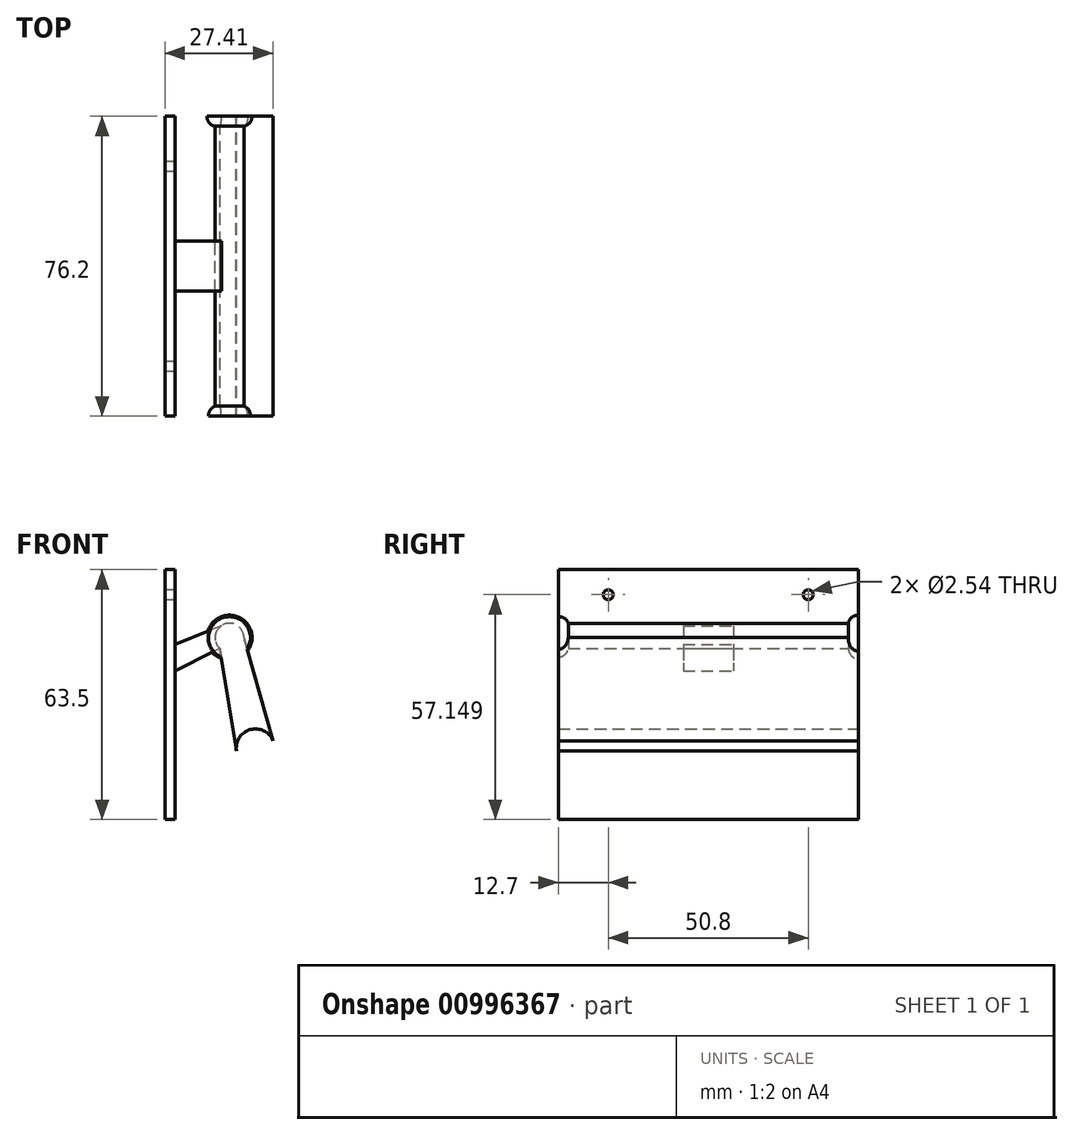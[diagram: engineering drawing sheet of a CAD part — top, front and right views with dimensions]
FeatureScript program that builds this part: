
annotation { "Feature Type Name" : "Feature", "Feature Type Description" : "" }
export const myFeature = defineFeature(function(context is Context, id is Id, definition is map)
    precondition{}
    {
        {
            var Q0;
            Q0=qCreatedBy(makeId("Front.planeOp"),FACE);
            var sketch = newSketch(context, id + "F0", { "sketchPlane" : qUnion([Q0])});
            skLineSegment(sketch, "E0.bottom", {"start": v(-19.93, 54.34) * mm, "end": v(-17.39, 54.34) * mm});
            skLineSegment(sketch, "E0.top", {"start": v(-19.93, -9.16) * mm, "end": v(-17.39, -9.16) * mm});
            skLineSegment(sketch, "E0.left", {"start": v(-19.93, 54.34) * mm, "end": v(-19.93, -9.16) * mm});
            skLineSegment(sketch, "E0.right", {"start": v(-17.39, 54.34) * mm, "end": v(-17.39, -9.16) * mm});
            skCircle(sketch, "E1", {"center": v(-3.57, 37.05) * mm, "radius": 3.67 * mm});
            skCircle(sketch, "E2", {"center": v(3, 9.03) * mm, "radius": 4.85 * mm});
            skLineSegment(sketch, "E3", {"start": v(0.1, 37.05) * mm, "end": v(7.78, 9.8) * mm});
            skLineSegment(sketch, "E4", {"start": v(-6.03, 34.33) * mm, "end": v(-1.53, 6.59) * mm});
            skLineSegment(sketch, "E5", {"start": v(-5.63, 40.09) * mm, "end": v(-17.39, 35.29) * mm});
            skLineSegment(sketch, "E6", {"start": v(-6.03, 34.33) * mm, "end": v(-17.39, 28.66) * mm});
            skSolve(sketch);
        }
        {
            var Q0;
            {var subQ1=sQuery(id+"F0.wireOp",EDGE,"E0.bottom");Q0=makeQuery(id+"F0.imprint","IMPRINT",FACE,{"disambiguationData":[TD([[makeQuery(id+"F0.imprint","IMPRINT",EDGE,{"derivedFrom":subQ1}),-1.0]])]});}
            var Q1;
            {var subQ0=sQuery(id+"F0.wireOp",EDGE,"E1");var subQ1=makeQuery(id+"F0.imprint","INTERSECT",VERTEX,{"derivedFrom":[subQ0,sQuery(id+"F0.wireOp",EDGE,"E3")]});Q1=makeQuery(id+"F0.imprint","IMPRINT",FACE,{"disambiguationData":[TD([[makeQuery(id+"F0.imprint","IMPRINT",EDGE,{"disambiguationData":[TD([[subQ1,-1.0]])],"derivedFrom":subQ0}),1.0]])]});}
            var Q2;
            {var subQ3=sQuery(id+"F0.wireOp",EDGE,"E4");var subQ5=sQuery(id+"F0.wireOp",EDGE,"E2");var subQ6=makeQuery(id+"F0.imprint","INTERSECT",VERTEX,{"derivedFrom":[subQ5,subQ3]});Q2=makeQuery(id+"F0.imprint","IMPRINT",FACE,{"disambiguationData":[TD([[makeQuery(id+"F0.imprint","IMPRINT",EDGE,{"disambiguationData":[TD([[subQ6,1.0]])],"derivedFrom":subQ5}),-1.0]])]});}
            extrude(context, id + "F1", {"entities" : qUnion([Q0, Q1, Q2]), "endBound" : BoundingType.SYMMETRIC, "depth" : 76.2 * mm, "offsetDistance" : 25.4 * mm});
        }
        {
            var Q0;
            {var subQ0=sQuery(id+"F0.wireOp",EDGE,"E5");Q0=makeQuery(id+"F0.imprint","IMPRINT",FACE,{"disambiguationData":[TD([[makeQuery(id+"F0.imprint","IMPRINT",EDGE,{"derivedFrom":subQ0}),1.0]])]});}
            extrude(context, id + "F2", {"entities" : qUnion([Q0]), "endBound" : BoundingType.SYMMETRIC, "depth" : 12.7 * mm, "offsetDistance" : 25.4 * mm});
        }
        {
            var Q0;
            Q0=makeQuery(id+"F1.opExtrude","SWEPT_FACE",FACE,{"disambiguationData":[OSD([sQuery(id+"F0.wireOp",EDGE,"E0.right")])]});
            var sketch = newSketch(context, id + "F3", { "sketchPlane" : qUnion([Q0])});
            skCircle(sketch, "E7", {"center": v(-25.4, 47.99) * mm, "radius": 1.27 * mm});
            skCircle(sketch, "E8", {"center": v(25.4, 47.99) * mm, "radius": 1.27 * mm});
            skSolve(sketch);
        }
        {
            var Q0;
            Q0=makeQuery(id+"F3.imprint","IMPRINT",FACE,{"disambiguationData":[TD([[makeQuery(id+"F3.imprint","IMPRINT",EDGE,{"derivedFrom":sQuery(id+"F3.wireOp",EDGE,"E7")}),1.0]])]});
            var Q1;
            Q1=sQuery(id+"F3.wireOp",EDGE,"E7");
            extrude(context, id + "F4", {"entities" : qUnion([Q0]), "operationType" : NewBodyOperationType.REMOVE, "surfaceEntities" : qUnion([Q1]), "endBound" : BoundingType.THROUGH_ALL, "oppositeDirection" : true, "depth" : 25.4 * mm, "offsetDistance" : 25.4 * mm});
        }
        {
            var Q0;
            Q0=makeQuery(id+"F3.imprint","IMPRINT",FACE,{"disambiguationData":[TD([[makeQuery(id+"F3.imprint","IMPRINT",EDGE,{"derivedFrom":sQuery(id+"F3.wireOp",EDGE,"E8")}),1.0]])]});
            var Q1;
            Q1=sQuery(id+"F3.wireOp",EDGE,"E8");
            extrude(context, id + "F5", {"entities" : qUnion([Q0]), "operationType" : NewBodyOperationType.REMOVE, "surfaceEntities" : qUnion([Q1]), "endBound" : BoundingType.THROUGH_ALL, "oppositeDirection" : true, "depth" : 25.4 * mm, "offsetDistance" : 25.4 * mm});
        }
        {
            var Q0;
            Q0=makeQuery(id+"F1.opExtrude","CAP_FACE",FACE,{"disambiguationData":[OSD([sQuery(id+"F0.wireOp",EDGE,"E1"),sQuery(id+"F0.wireOp",EDGE,"E2"),sQuery(id+"F0.wireOp",EDGE,"E3"),sQuery(id+"F0.wireOp",EDGE,"E4")])],"isStart":true});
            var sketch = newSketch(context, id + "F6", { "sketchPlane" : qUnion([Q0])});
            skCircle(sketch, "E9", {"center": v(3.57, 37.05) * mm, "radius": 5.72 * mm});
            skSolve(sketch);
        }
        {
            var Q0;
            {var subQ5=makeQuery(id+"F1.opExtrude","CAP_EDGE",EDGE,{"disambiguationData":[OSD([sQuery(id+"F0.wireOp",EDGE,"E1")])],"isStart":true});Q0=makeQuery(id+"F6.imprint","IMPRINT",FACE,{"disambiguationData":[TD([[makeQuery(id+"F6.imprint","IMPRINT",EDGE,{"derivedFrom":subQ5}),1.0]])]});}
            extrude(context, id + "F7", {"entities" : qUnion([Q0]), "operationType" : NewBodyOperationType.ADD, "oppositeDirection" : true, "depth" : 2.54 * mm, "offsetDistance" : 25.4 * mm});
        }
        {
            var Q0;
            Q0=makeQuery(id+"F7.opExtrude","CAP_EDGE",EDGE,{"disambiguationData":[OSD([sQuery(id+"F6.wireOp",EDGE,"E9")])],"isStart":false});
            fillet(context, id + "F8", {"entities" : qUnion([Q0]), "tangentPropagation" : true, "radius" : 2.54 * mm, "defaultsChanged" : true, "vertexSettings" : [], "allowEdgeOverflow" : false});
        }
        {
            var Q0;
            Q0=makeQuery(id+"F1.opExtrude","CAP_FACE",FACE,{"disambiguationData":[OSD([sQuery(id+"F0.wireOp",EDGE,"E1"),sQuery(id+"F0.wireOp",EDGE,"E2"),sQuery(id+"F0.wireOp",EDGE,"E3"),sQuery(id+"F0.wireOp",EDGE,"E4")])],"isStart":false});
            var sketch = newSketch(context, id + "F9", { "sketchPlane" : qUnion([Q0])});
            skCircle(sketch, "E10", {"center": v(-3.57, 37.05) * mm, "radius": 5.33 * mm});
            skSolve(sketch);
        }
        {
            var Q0;
            Q0 = qSketchRegion(id + "F9", true);
            extrude(context, id + "F10", {"entities" : qUnion([Q0]), "operationType" : NewBodyOperationType.ADD, "oppositeDirection" : true, "depth" : 2.54 * mm, "offsetDistance" : 25.4 * mm});
        }
        {
            var Q0;
            Q0=makeQuery(id+"F10.opExtrude","CAP_EDGE",EDGE,{"disambiguationData":[OSD([sQuery(id+"F9.wireOp",EDGE,"E10")])],"isStart":false});
            fillet(context, id + "F11", {"entities" : qUnion([Q0]), "tangentPropagation" : true, "radius" : 2.54 * mm, "defaultsChanged" : true, "vertexSettings" : [], "allowEdgeOverflow" : false});
        }
    });
